# Revit family: Louver-Flanged_Frame-Carnes-Rectangular-Drainable_Blade-FTAB
name_source: partatom
category: Air Terminals
revit_build: Autodesk Revit MEP 2012 (Build: 20110916_2132(x64)
units: mm (PartAtom-declared; Revit-internal decimal feet)

## types (1)
- (See Type Catalog)
    04 CSI = 08 91 00
    95 CSI = 10200
    Airflow = 0 CFM
    Assembly Code = D3090700
    Blade Material = Aluminum - Carnes - Extruded
    Catalog URL = http://www.carnes.com
    Connector Description 1 = Duct Connetor
    Default Elevation = 48 "
    Description = Extruded Aluminum Drainable Blade Louvers
    Frame Material = Aluminum - Carnes - Extruded
    Free Area = 0 SF
    Free Area Note = See Spec Sheet URL
    Louver Height = 24 "
    Louver Length = 2.16 "
    Louver Width = 24 "
    Manufacturer = Carnes Company
    Manufacturer Fax = 608-845-6470
    Maximum Horinzontal Size = 120"W x 84"H
    Maximum Size Note = Drainable blade louvers should be limited to 10’ maximum section widths (no more than 10’ between vertical downspouts) to enable the drainable design to function effectively.
    Maximum Vertical Size = 84"W x 120"H
    Meets Building Code Standards = Licensed to bear the AMCA seal
    Minimum Size = 12"W x 12"H
    Model = FTAB
    Outside Height = 26 "
    Outside Width = 26 "
    Point of Water Penetration = 805 FPM
    Pressure Drop = 0.00 Pa
    Product Line = Extruded Aluminum Drainable Blade Louvers
    Product Page URL = http://www.carnes.com
    Specifications  URL = http://www.carnes.com
    Subcategory = Louvers and Dampers
    URL = http://www.carnes.com
    ecoScorecard Product Page = http://ecoscorecard.com

## geometry (parser evidence)
native form markers: Blend x2, Sweep x5
no freeform markers — native parametric forms only
